SOLIDWORKS PART (.sldprt)
format: sldprt  version: not decoded by parser v0  size: 288,768 bytes
history: native  units: mm
features: sketch x4, cut_extrude x3, material x1, plane x1, extrude x1 (+11 scaffold rows collapsed)
feature tree (21):
  scaffold x11  (default folders/planes/origin — collapsed)
  material  "Material <not specified>"
  plane  "Plane1"  Offset=2mm
  sketch  "Sketch2"  dims[D1=31.75mm]
  extrude  "Boss-Extrude1"  Depth=6.35mm
  sketch  "Sketch5"  dims[D1=6.0]
  cut_extrude  "Cut-Extrude2"  [1 undecoded]
  sketch  "Sketch7"  dims[D1=7.0]
  cut_extrude  "Cut-Extrude4"  [1 undecoded]
  sketch  "Sketch6"  dims[c1.D1=~6.679186mm c2.D1=7.0]
  cut_extrude  "Cut-Extrude3"  [1 undecoded]
decode coverage: 5 of 8 modeling features carry decoded parameters
note: ~ marks probable driven/reference dimensions
note: 3 parameter values undecoded
summary: no parameter record found for 3 features
note: suppression state not decoded; provenance and decode notes live in map.json
